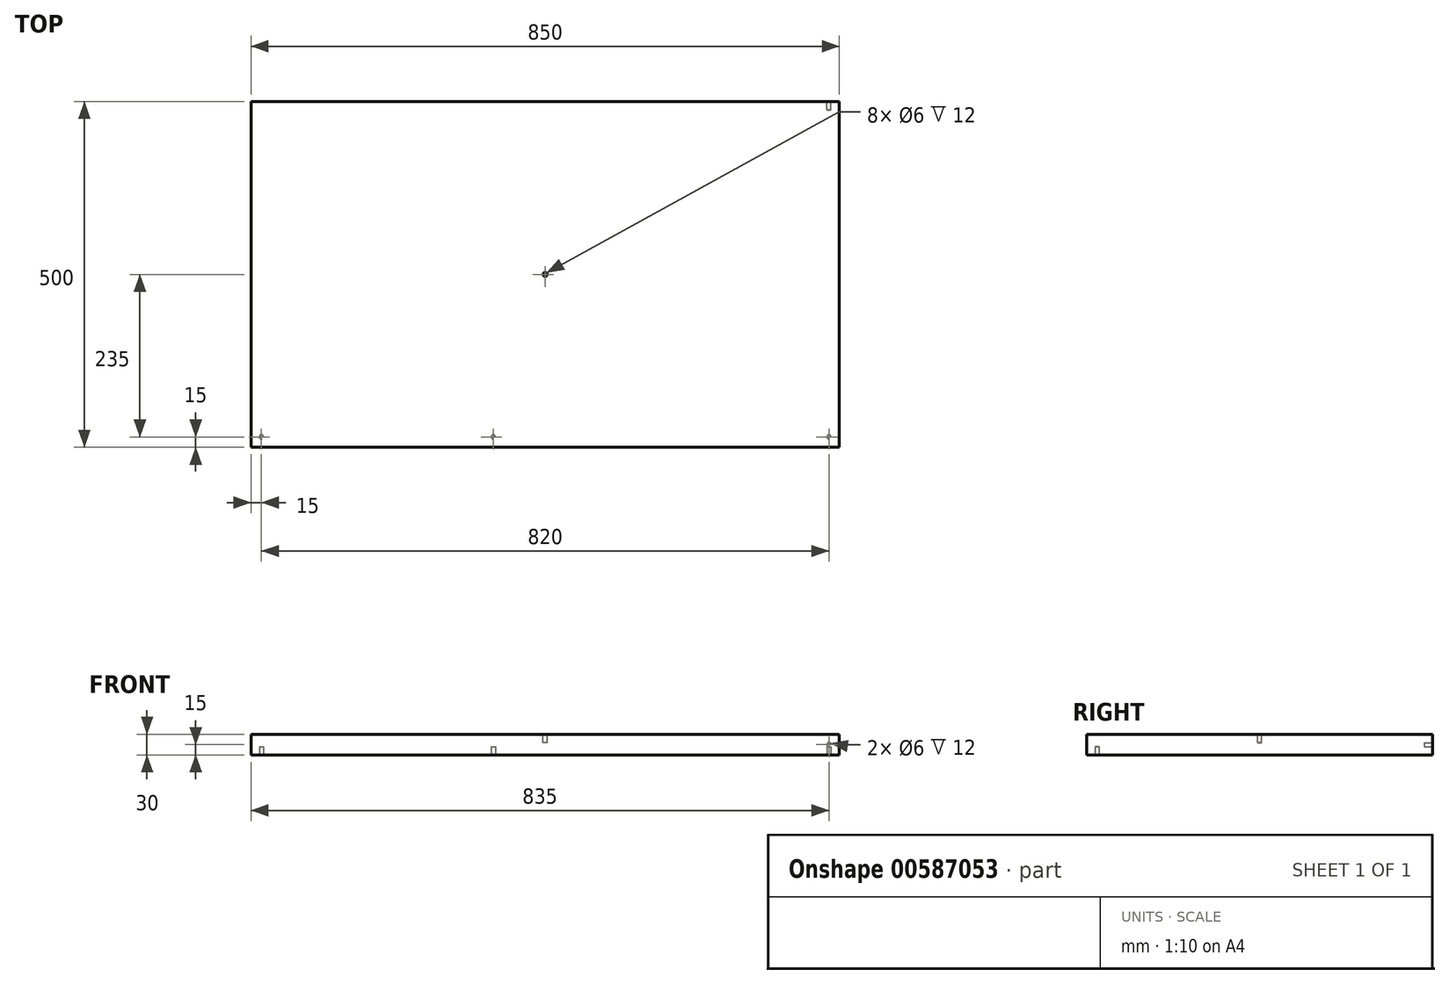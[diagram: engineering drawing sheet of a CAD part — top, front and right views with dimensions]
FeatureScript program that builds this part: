
annotation { "Feature Type Name" : "Feature", "Feature Type Description" : "" }
export const myFeature = defineFeature(function(context is Context, id is Id, definition is map)
    precondition{}
    {
        {
            var Q0;
            Q0=qCreatedBy(makeId("Top.planeOp"),FACE);
            var sketch = newSketch(context, id + "F0", { "sketchPlane" : qUnion([Q0])});
            skLineSegment(sketch, "E0.bottom", {"start": v(0, 0) * mm, "end": v(850, 0) * mm});
            skLineSegment(sketch, "E0.top", {"start": v(0, 500) * mm, "end": v(850, 500) * mm});
            skLineSegment(sketch, "E0.left", {"start": v(0, 0) * mm, "end": v(0, 500) * mm});
            skLineSegment(sketch, "E0.right", {"start": v(850, 0) * mm, "end": v(850, 500) * mm});
            skSolve(sketch);
        }
        {
            var Q0;
            Q0=makeQuery(id+"F0.imprint","IMPRINT",FACE,{"disambiguationData":[TD([[makeQuery(id+"F0.imprint","IMPRINT",EDGE,{"derivedFrom":sQuery(id+"F0.wireOp",EDGE,"E0.bottom")}),1.0]])]});
            extrude(context, id + "F1", {"entities" : qUnion([Q0]), "depth" : 30 * mm, "offsetDistance" : 25 * mm});
        }
        {
            var Q0;
            Q0=makeQuery(id+"F1.opExtrude","CAP_FACE",FACE,{"disambiguationData":[OSD([sQuery(id+"F0.wireOp",EDGE,"E0.bottom"),sQuery(id+"F0.wireOp",EDGE,"E0.top"),sQuery(id+"F0.wireOp",EDGE,"E0.left"),sQuery(id+"F0.wireOp",EDGE,"E0.right")])],"isStart":true});
            var sketch = newSketch(context, id + "F2", { "sketchPlane" : qUnion([Q0])});
            skCircle(sketch, "E1", {"center": v(835, -15) * mm, "radius": 3 * mm});
            skSolve(sketch);
        }
        {
            var Q0;
            Q0=makeQuery(id+"F2.imprint","IMPRINT",FACE,{"disambiguationData":[TD([[makeQuery(id+"F2.imprint","IMPRINT",EDGE,{"derivedFrom":sQuery(id+"F2.wireOp",EDGE,"E1")}),1.0]])]});
            extrude(context, id + "F3", {"entities" : qUnion([Q0]), "operationType" : NewBodyOperationType.REMOVE, "oppositeDirection" : true, "depth" : 12 * mm, "offsetDistance" : 25 * mm});
        }
        {
            var Q0;
            Q0=makeQuery(id+"F1.opExtrude","CAP_FACE",FACE,{"disambiguationData":[OSD([sQuery(id+"F0.wireOp",EDGE,"E0.bottom"),sQuery(id+"F0.wireOp",EDGE,"E0.top"),sQuery(id+"F0.wireOp",EDGE,"E0.left"),sQuery(id+"F0.wireOp",EDGE,"E0.right")])],"isStart":true});
            var sketch = newSketch(context, id + "F4", { "sketchPlane" : qUnion([Q0])});
            skCircle(sketch, "E2", {"center": v(15, -15) * mm, "radius": 3 * mm});
            skSolve(sketch);
        }
        {
            var Q0;
            Q0=makeQuery(id+"F4.imprint","IMPRINT",FACE,{"disambiguationData":[TD([[makeQuery(id+"F4.imprint","IMPRINT",EDGE,{"derivedFrom":sQuery(id+"F4.wireOp",EDGE,"E2")}),1.0]])]});
            extrude(context, id + "F5", {"entities" : qUnion([Q0]), "operationType" : NewBodyOperationType.REMOVE, "oppositeDirection" : true, "depth" : 12 * mm, "offsetDistance" : 25 * mm});
        }
        {
            var Q0;
            Q0=makeQuery(id+"F1.opExtrude","CAP_FACE",FACE,{"disambiguationData":[OSD([sQuery(id+"F0.wireOp",EDGE,"E0.bottom"),sQuery(id+"F0.wireOp",EDGE,"E0.top"),sQuery(id+"F0.wireOp",EDGE,"E0.left"),sQuery(id+"F0.wireOp",EDGE,"E0.right")])],"isStart":true});
            var sketch = newSketch(context, id + "F6", { "sketchPlane" : qUnion([Q0])});
            skCircle(sketch, "E3", {"center": v(350, -15) * mm, "radius": 3 * mm});
            skSolve(sketch);
        }
        {
            var Q0;
            Q0=makeQuery(id+"F6.imprint","IMPRINT",FACE,{"disambiguationData":[TD([[makeQuery(id+"F6.imprint","IMPRINT",EDGE,{"derivedFrom":sQuery(id+"F6.wireOp",EDGE,"E3")}),1.0]])]});
            extrude(context, id + "F7", {"entities" : qUnion([Q0]), "operationType" : NewBodyOperationType.REMOVE, "oppositeDirection" : true, "depth" : 12 * mm, "offsetDistance" : 25 * mm});
        }
        {
            var Q0;
            Q0=makeQuery(id+"F1.opExtrude","CAP_FACE",FACE,{"disambiguationData":[OSD([sQuery(id+"F0.wireOp",EDGE,"E0.bottom"),sQuery(id+"F0.wireOp",EDGE,"E0.top"),sQuery(id+"F0.wireOp",EDGE,"E0.left"),sQuery(id+"F0.wireOp",EDGE,"E0.right")])],"isStart":false});
            var sketch = newSketch(context, id + "F8", { "sketchPlane" : qUnion([Q0])});
            skCircle(sketch, "E4", {"center": v(425, 250) * mm, "radius": 3 * mm});
            skPoint(sketch, "E4.centerSnap0", {"position": v(0, 250) * mm});
            skPoint(sketch, "E4.centerSnap1", {"position": v(425, 500) * mm});
            skSolve(sketch);
        }
        {
            var Q0;
            Q0=makeQuery(id+"F8.imprint","IMPRINT",FACE,{"disambiguationData":[TD([[makeQuery(id+"F8.imprint","IMPRINT",EDGE,{"derivedFrom":sQuery(id+"F8.wireOp",EDGE,"E4")}),1.0]])]});
            extrude(context, id + "F9", {"entities" : qUnion([Q0]), "operationType" : NewBodyOperationType.REMOVE, "oppositeDirection" : true, "depth" : 12 * mm, "offsetDistance" : 25 * mm});
        }
        {
            var Q0;
            Q0=makeQuery(id+"F1.opExtrude","SWEPT_FACE",FACE,{"disambiguationData":[OSD([sQuery(id+"F0.wireOp",EDGE,"E0.top")])]});
            var sketch = newSketch(context, id + "F10", { "sketchPlane" : qUnion([Q0])});
            skCircle(sketch, "E5", {"center": v(-835, 15) * mm, "radius": 3 * mm});
            skPoint(sketch, "E5.centerSnap0", {"position": v(-850, 15) * mm});
            skSolve(sketch);
        }
        {
            var Q0;
            Q0=makeQuery(id+"F10.imprint","IMPRINT",FACE,{"disambiguationData":[TD([[makeQuery(id+"F10.imprint","IMPRINT",EDGE,{"derivedFrom":sQuery(id+"F10.wireOp",EDGE,"E5")}),1.0]])]});
            extrude(context, id + "F11", {"entities" : qUnion([Q0]), "operationType" : NewBodyOperationType.REMOVE, "oppositeDirection" : true, "depth" : 12 * mm, "offsetDistance" : 25 * mm});
        }
    });
